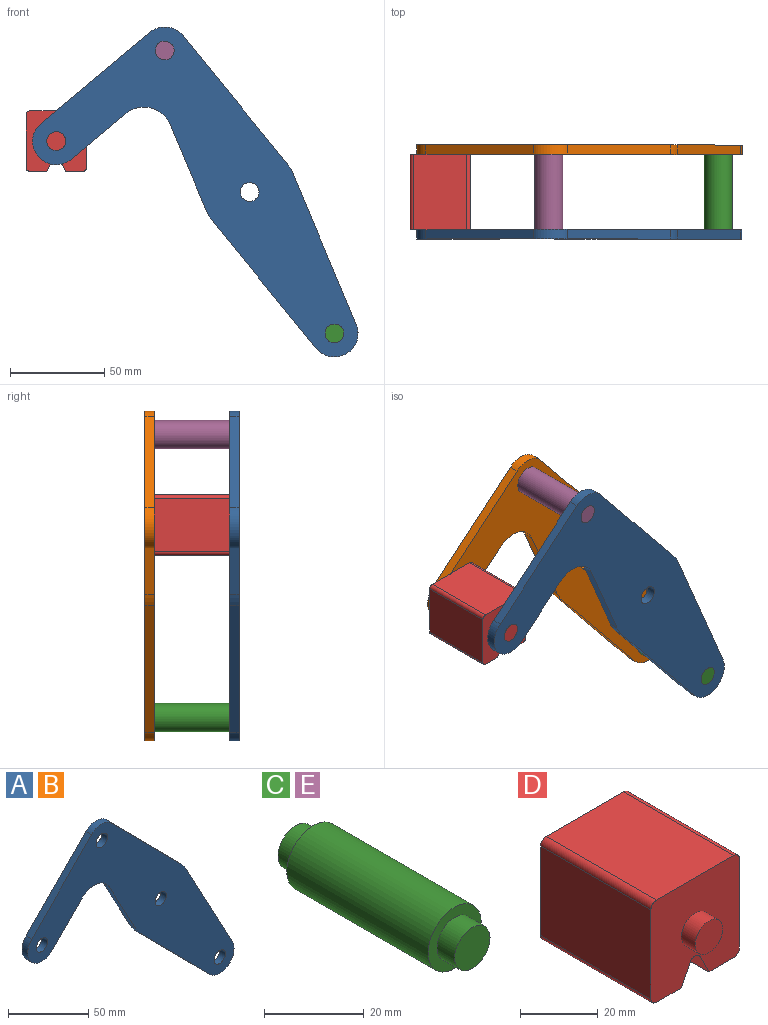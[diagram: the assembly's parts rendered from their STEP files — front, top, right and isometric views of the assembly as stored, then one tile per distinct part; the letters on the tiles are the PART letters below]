
ASSEMBLY  parts=5 mates=3
PART A: 18 faces, bbox 181.7x5x165.8 mm
  f0: plane 43.49x23.35mm, normal (-0.88,0,-0.47), area 246.8mm2, adj f1,f14,f16,f17
  f1: cylinder r=25mm len=5.75mm, axis (0,1,0), area 35.8mm2, adj f0,f2,f16,f17
  f2: plane 61.6x60.87mm, normal (-0.71,0,-0.7), area 433mm2, adj f1,f3,f16,f17
  f3: cylinder r=12.5mm len=21.39mm, axis (0,1,0), area 178.4mm2, adj f2,f4,f16,f17
  f4: plane 76.3x40.96mm, normal (0.88,0,0.47), area 433mm2, adj f3,f5,f16,f17
  f5: cylinder r=25mm len=5.75mm, axis (0,1,0), area 35.8mm2, adj f4,f6,f16,f17
  f6: plane 61.6x60.87mm, normal (0.71,0,0.7), area 433mm2, adj f5,f7,f16,f17
  f7: cylinder r=12.5mm len=17.78mm, axis (0,1,0), area 98.9mm2, adj f6,f8,f16,f17
  f8: plane 53.35x52.71mm, normal (-0.71,0,0.7), area 375mm2, adj f7,f9,f16,f17
  f9: cylinder r=12.5mm len=21.39mm, axis (0,1,0), area 196.3mm2, adj f8,f10,f16,f17
  f10: plane 26.86x26.54mm, normal (0.71,0,-0.7), area 188.8mm2, adj f9,f14,f16,f17
  f11: cylinder r=5mm len=10mm, axis (0,1,0), area 157.1mm2, adj f16,f17
  f12: cylinder r=5mm len=10mm, axis (0,1,0), area 157.1mm2, adj f16,f17
  f13: cylinder r=5mm len=10mm, axis (0,1,0), area 157.1mm2, adj f16,f17
  f14: cylinder r=15mm len=23.89mm, axis (0,1,0), area 140.2mm2, adj f0,f10,f16,f17
  f15: cylinder r=5mm len=10mm, axis (0,1,0), area 157.1mm2, adj f16,f17
  f16: plane 181.66x165.78mm, normal (0,-1,0), area 8710.1mm2, adj f0,f1,f2,f3,f4,f5,f6,f7
  f17: plane 181.66x165.78mm, normal (0,1,0), area 8710.1mm2, adj f0,f1,f2,f3,f4,f5,f6,f7
PART B: same geometry as A
PART C: 7 faces, bbox 15x50x15 mm
  f0: cylinder r=7.5mm len=40mm, axis (0,-1,0), area 1885mm2, adj f2,f5
  f1: cylinder r=5mm len=10mm, axis (0,1,0), area 157.1mm2, adj f2,f3
  f2: plane 15x15mm, normal (0,-1,0), area 98.2mm2, adj f0,f1
  f3: plane 10x10mm, normal (0,-1,0), area 78.5mm2, adj f1
  f4: cylinder r=5mm len=10mm, axis (0,-1,0), area 157.1mm2, adj f5,f6
  f5: plane 15x15mm, normal (0,1,0), area 98.2mm2, adj f0,f4
  f6: plane 10x10mm, normal (0,1,0), area 78.5mm2, adj f4
PART D: 18 faces, bbox 32.1x50x32.1 mm
  f0: plane 40x28.08mm, normal (1,0,0), area 1123.1mm2, adj f4,f10,f13,f14
  f1: plane 40x9.04mm, normal (0,0,-1), area 361.6mm2, adj f2,f4,f10,f14
  f2: plane 40x6.42mm, normal (-0.89,0,-0.45), area 287.2mm2, adj f1,f4,f10,f15
  f3: plane 40x6.42mm, normal (0.89,0,-0.45), area 287.2mm2, adj f4,f5,f10,f15
  f4: plane 32.08x32.08mm, normal (0,-1,0), area 900.6mm2, adj f0,f1,f2,f3,f5,f6,f7,f9
  f5: plane 40x9.04mm, normal (0,0,-1), area 361.6mm2, adj f3,f4,f10,f16
  f6: plane 40x28.08mm, normal (0,0,1), area 1123.1mm2, adj f4,f10,f13,f17
  f7: plane 40x28.08mm, normal (-1,0,0), area 1123.1mm2, adj f4,f10,f16,f17
  f8: plane 10x10mm, normal (0,-1,0), area 78.5mm2, adj f9
  f9: cylinder r=5mm len=10mm, axis (0,1,0), area 157.1mm2, adj f4,f8
  f10: plane 32.08x32.08mm, normal (0,1,0), area 900.6mm2, adj f0,f1,f2,f3,f5,f6,f7,f12
  f11: plane 10x10mm, normal (0,1,0), area 78.5mm2, adj f12
  f12: cylinder r=5mm len=10mm, axis (0,-1,0), area 157.1mm2, adj f10,f11
  f13: cylinder r=2mm len=40mm, axis (0,1,0), area 125.7mm2, adj f0,f4,f6,f10
  f14: cylinder r=2mm len=40mm, axis (0,-1,0), area 125.7mm2, adj f0,f1,f4,f10
  f15: cylinder r=2mm len=40mm, axis (0,1,0), area 177.1mm2, adj f2,f3,f4,f10
  f16: cylinder r=2mm len=40mm, axis (0,1,0), area 125.7mm2, adj f4,f5,f7,f10
  f17: cylinder r=2mm len=40mm, axis (0,-1,0), area 125.7mm2, adj f4,f6,f7,f10
PART E: same geometry as C
PLACE A rot(axis=(0,1,0),5.5deg) t=(0,-20,0)mm fixed
PLACE B rot(axis=(0,1,0),5.5deg) t=(0,25,0)mm
PLACE C rot(axis=(0,1,0),5.5deg) t=(90.03,-20,-150.06)mm
PLACE D t=(2.11,-20,9.92)mm
PLACE E rot(axis=(0,1,0),5.5deg) t=(0,-20,0)mm
MATE fastened C.f0 <-> B.f3  axis (0,1,0) through (45.02,20,-75.03)mm
MATE fastened B.f7 <-> E.f0  axis (0,-1,0) through (-45.02,20,75.03)mm
MATE revolute D.f9 <-> A.f9  axis (0,-1,0) through (-102.58,-20,26.96)mm
